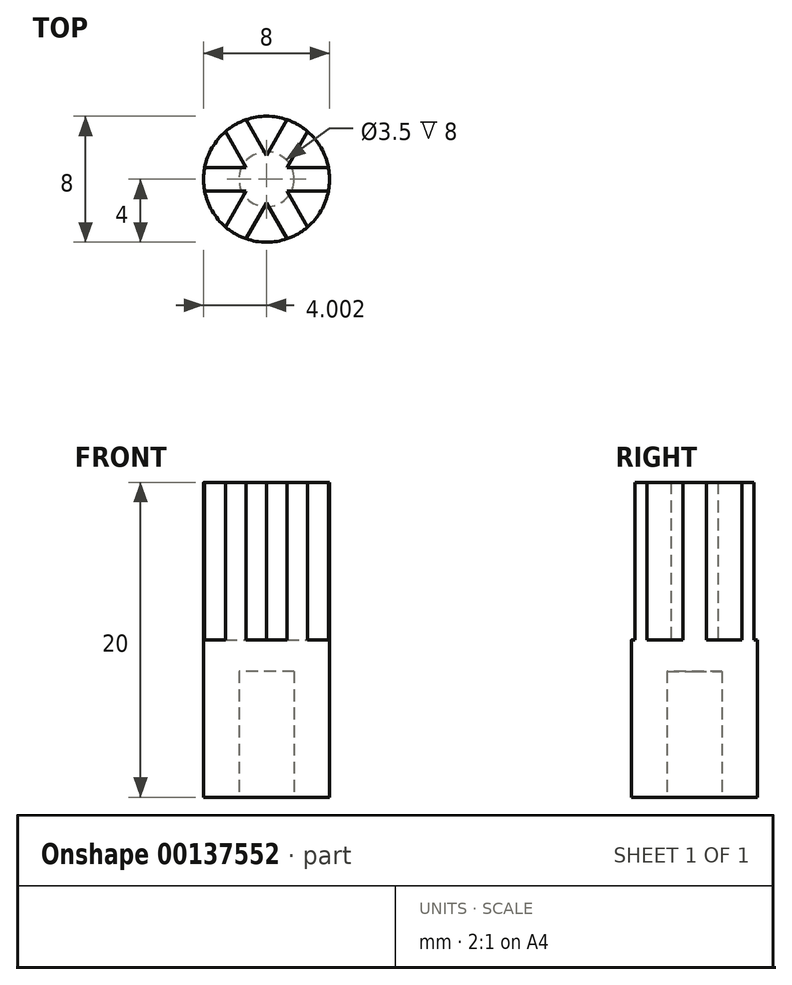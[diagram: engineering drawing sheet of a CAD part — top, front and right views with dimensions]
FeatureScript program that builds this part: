
annotation { "Feature Type Name" : "Feature", "Feature Type Description" : "" }
export const myFeature = defineFeature(function(context is Context, id is Id, definition is map)
    precondition{}
    {
        {
            var Q0;
            Q0=qCreatedBy(makeId("Top.planeOp"),FACE);
            var sketch = newSketch(context, id + "F0", { "sketchPlane" : qUnion([Q0])});
            skCircle(sketch, "E0", {"center": v(-17.52, 0) * mm, "radius": 4 * mm});
            skCircle(sketch, "E1", {"center": v(-17.52, 0) * mm, "radius": 1.75 * mm});
            skSolve(sketch);
        }
        {
            var Q0;
            Q0=makeQuery(id+"F0.imprint","IMPRINT",FACE,{"disambiguationData":[TD([[makeQuery(id+"F0.imprint","IMPRINT",EDGE,{"derivedFrom":sQuery(id+"F0.wireOp",EDGE,"E0")}),1.0]])]});
            var Q1;
            Q1=makeQuery(id+"F0.imprint","IMPRINT",FACE,{"disambiguationData":[TD([[makeQuery(id+"F0.imprint","IMPRINT",EDGE,{"derivedFrom":sQuery(id+"F0.wireOp",EDGE,"E1")}),1.0]])]});
            extrude(context, id + "F1", {"entities" : qUnion([Q0, Q1]), "depth" : 10 * mm});
        }
        {
            var Q0;
            Q0=makeQuery(id+"F1.opExtrude","CAP_FACE",FACE,{"disambiguationData":[OSD([sQuery(id+"F0.wireOp",EDGE,"E0")])],"isStart":false});
            var sketch = newSketch(context, id + "F2", { "sketchPlane" : qUnion([Q0])});
            skPoint(sketch, "E2.center", {"position": v(-17.52, 0) * mm});
            skLineSegment(sketch, "E3", {"start": v(-13.52, 0) * mm, "end": v(-21.52, 0) * mm});
            skLineSegment(sketch, "E4", {"start": v(-13.59, 0.75) * mm, "end": v(-21.45, 0.75) * mm});
            skLineSegment(sketch, "E5", {"start": v(-21.45, -0.75) * mm, "end": v(-13.59, -0.75) * mm});
            skLineSegment(sketch, "E6.1.0", {"start": v(-20.13, 3.03) * mm, "end": v(-16.2, -3.78) * mm});
            skLineSegment(sketch, "E6.1.1", {"start": v(-14.9, -3.03) * mm, "end": v(-18.83, 3.78) * mm});
            skLineSegment(sketch, "E6.2.0", {"start": v(-18.83, -3.78) * mm, "end": v(-14.9, 3.03) * mm});
            skLineSegment(sketch, "E6.2.1", {"start": v(-16.2, 3.78) * mm, "end": v(-20.13, -3.03) * mm});
            skSolve(sketch);
        }
        {
            var Q0;
            Q0=makeQuery(id+"F0.imprint","IMPRINT",FACE,{"disambiguationData":[TD([[makeQuery(id+"F0.imprint","IMPRINT",EDGE,{"derivedFrom":sQuery(id+"F0.wireOp",EDGE,"E1")}),1.0]])]});
            extrude(context, id + "F3", {"entities" : qUnion([Q0]), "operationType" : NewBodyOperationType.REMOVE, "depth" : 8 * mm});
        }
        {
            var Q0;
            {var subQ0=sQuery(id+"F2.wireOp",EDGE,"E3");Q0=makeQuery(id+"F2.imprint","IMPRINT",FACE,{"disambiguationData":[TD([[makeQuery(id+"F2.imprint","IMPRINT",EDGE,{"derivedFrom":subQ0}),-1.0]])]});}
            var Q1;
            {var subQ0=sQuery(id+"F2.wireOp",EDGE,"E3");Q1=makeQuery(id+"F2.imprint","IMPRINT",FACE,{"disambiguationData":[TD([[makeQuery(id+"F2.imprint","IMPRINT",EDGE,{"derivedFrom":subQ0}),1.0]])]});}
            var Q2;
            {var subQ0=sQuery(id+"F2.wireOp",EDGE,"E6.2.1");var subQ1=sQuery(id+"F2.wireOp",EDGE,"E4");var subQ2=makeQuery(id+"F2.imprint","INTERSECT",VERTEX,{"derivedFrom":[subQ1,subQ0]});Q2=makeQuery(id+"F2.imprint","IMPRINT",FACE,{"disambiguationData":[TD([[makeQuery(id+"F2.imprint","IMPRINT",EDGE,{"disambiguationData":[TD([[subQ2,-1.0]])],"derivedFrom":subQ1}),1.0]])]});}
            var Q3;
            {var subQ0=sQuery(id+"F2.wireOp",EDGE,"E6.2.0");var subQ1=sQuery(id+"F2.wireOp",EDGE,"E4");var subQ2=makeQuery(id+"F2.imprint","INTERSECT",VERTEX,{"derivedFrom":[subQ1,subQ0]});Q3=makeQuery(id+"F2.imprint","IMPRINT",FACE,{"disambiguationData":[TD([[makeQuery(id+"F2.imprint","IMPRINT",EDGE,{"disambiguationData":[TD([[subQ2,-1.0]])],"derivedFrom":subQ1}),1.0]])]});}
            var Q4;
            {var subQ0=sQuery(id+"F2.wireOp",EDGE,"E6.2.0");var subQ1=sQuery(id+"F2.wireOp",EDGE,"E5");var subQ2=makeQuery(id+"F2.imprint","INTERSECT",VERTEX,{"derivedFrom":[subQ1,subQ0]});Q4=makeQuery(id+"F2.imprint","IMPRINT",FACE,{"disambiguationData":[TD([[makeQuery(id+"F2.imprint","IMPRINT",EDGE,{"disambiguationData":[TD([[subQ2,-1.0]])],"derivedFrom":subQ1}),1.0]])]});}
            var Q5;
            {var subQ0=sQuery(id+"F2.wireOp",EDGE,"E6.2.1");var subQ1=sQuery(id+"F2.wireOp",EDGE,"E5");var subQ2=makeQuery(id+"F2.imprint","INTERSECT",VERTEX,{"derivedFrom":[subQ1,subQ0]});Q5=makeQuery(id+"F2.imprint","IMPRINT",FACE,{"disambiguationData":[TD([[makeQuery(id+"F2.imprint","IMPRINT",EDGE,{"disambiguationData":[TD([[subQ2,-1.0]])],"derivedFrom":subQ1}),1.0]])]});}
            var Q6;
            {var subQ0=sQuery(id+"F2.wireOp",EDGE,"E6.1.0");var subQ1=sQuery(id+"F2.wireOp",EDGE,"E5");var subQ2=makeQuery(id+"F2.imprint","INTERSECT",VERTEX,{"derivedFrom":[subQ1,subQ0]});Q6=makeQuery(id+"F2.imprint","IMPRINT",FACE,{"disambiguationData":[TD([[makeQuery(id+"F2.imprint","IMPRINT",EDGE,{"disambiguationData":[TD([[subQ2,-1.0]])],"derivedFrom":subQ1}),-1.0]])]});}
            var Q7;
            {var subQ0=sQuery(id+"F2.wireOp",EDGE,"E6.2.0");var subQ1=sQuery(id+"F2.wireOp",EDGE,"E5");var subQ2=makeQuery(id+"F2.imprint","INTERSECT",VERTEX,{"derivedFrom":[subQ1,subQ0]});Q7=makeQuery(id+"F2.imprint","IMPRINT",FACE,{"disambiguationData":[TD([[makeQuery(id+"F2.imprint","IMPRINT",EDGE,{"disambiguationData":[TD([[subQ2,-1.0]])],"derivedFrom":subQ1}),-1.0]])]});}
            var Q8;
            {var subQ0=sQuery(id+"F2.wireOp",EDGE,"E6.2.1");var subQ3=sQuery(id+"F2.wireOp",EDGE,"E5");var subQ4=makeQuery(id+"F2.imprint","INTERSECT",VERTEX,{"derivedFrom":[subQ3,subQ0]});Q8=makeQuery(id+"F2.imprint","IMPRINT",FACE,{"disambiguationData":[TD([[makeQuery(id+"F2.imprint","IMPRINT",EDGE,{"disambiguationData":[TD([[subQ4,-1.0]])],"derivedFrom":subQ3}),-1.0]])]});}
            var Q9;
            {var subQ0=sQuery(id+"F2.wireOp",EDGE,"E6.1.1");var subQ1=sQuery(id+"F2.wireOp",EDGE,"E4");var subQ2=makeQuery(id+"F2.imprint","INTERSECT",VERTEX,{"derivedFrom":[subQ1,subQ0]});Q9=makeQuery(id+"F2.imprint","IMPRINT",FACE,{"disambiguationData":[TD([[makeQuery(id+"F2.imprint","IMPRINT",EDGE,{"disambiguationData":[TD([[subQ2,-1.0]])],"derivedFrom":subQ1}),-1.0]])]});}
            var Q10;
            {var subQ0=sQuery(id+"F2.wireOp",EDGE,"E6.2.1");var subQ1=sQuery(id+"F2.wireOp",EDGE,"E4");var subQ2=makeQuery(id+"F2.imprint","INTERSECT",VERTEX,{"derivedFrom":[subQ1,subQ0]});Q10=makeQuery(id+"F2.imprint","IMPRINT",FACE,{"disambiguationData":[TD([[makeQuery(id+"F2.imprint","IMPRINT",EDGE,{"disambiguationData":[TD([[subQ2,-1.0]])],"derivedFrom":subQ1}),-1.0]])]});}
            var Q11;
            {var subQ5=sQuery(id+"F2.wireOp",EDGE,"E6.2.0");var subQ7=sQuery(id+"F2.wireOp",EDGE,"E4");var subQ8=makeQuery(id+"F2.imprint","INTERSECT",VERTEX,{"derivedFrom":[subQ7,subQ5]});Q11=makeQuery(id+"F2.imprint","IMPRINT",FACE,{"disambiguationData":[TD([[makeQuery(id+"F2.imprint","IMPRINT",EDGE,{"disambiguationData":[TD([[subQ8,-1.0]])],"derivedFrom":subQ7}),-1.0]])]});}
            extrude(context, id + "F4", {"entities" : qUnion([Q0, Q1, Q2, Q3, Q4, Q5, Q6, Q7, Q8, Q9, Q10, Q11]), "operationType" : NewBodyOperationType.ADD, "depth" : 10 * mm});
        }
    });
